# Revit family: ZETA_Коробка_Клемная_КЗНА-48_IP43
name_source: partatom
category: Электрические приборы
units: mm (PartAtom-declared; Revit-internal decimal feet)

## family parameters
Всегда вертикально = Нет
На основе рабочей плоскости = Да
Общий = Нет
При загрузке вырезать с полостями = Нет
Размер круглого соединителя = Использовать диаметр
Сохранять ориентацию аннотаций = Нет
Тип детали = Нормальный
Точка принадлежности помещению = Да

## types (2) — shared parameters
ADSK_URL документации изделия = https://nzeta.ru
ADSK_URL страницы изделия = https://nzeta.ru
ADSK_Версия Revit = 2021
ADSK_Версия семейства = v.1
ADSK_Единица измерения = шт
ADSK_Завод-изготовитель = АО «ЗЭТА»
ADSK_Классификация нагрузок = Прочее
ADSK_Код изделия = zeta30313
ADSK_Количество = 1
ADSK_Количество фаз = 1
ADSK_Количество фаз числовое = 1
ADSK_Коэффициент мощности = 1
ADSK_Марка = KK КЗНА-48 У3 IP43
ADSK_Масса = 5.67
ADSK_Масса_Текст = 5,67
ADSK_Материал наименование = Сталь оцинкованная
ADSK_Наименование = Коробка с зажимами наборными КЗНА-48 У3 IP43 ГОФРОМАТИК
ADSK_Наименование краткое = КЗНА-48
ADSK_Напряжение = 230 В
ADSK_Номинальная мощность = 0 Вт
ADSK_Обозначение = KK
ADSK_Полная мощность = 0 В·А
ADSK_Размер_Высота = 107 мм
ADSK_Размер_Длина = 345 мм
ADSK_Размер_Ширина = 266 мм
ADSK_Степень защиты_IP = IP43
ADSK_Ток = 0 А
D1 = 25 мм
D2 = 32 мм
D3 = 20 мм
D4 = 40 мм
URL = https://nzeta.ru
Изготавливается по = ТУ 27.33.13.120-047-99856433-2020
Изготовитель = АО «ЗЭТА»
Климатическое исполнение = У3
Крышка_Длина = 190 мм
Крышка_Ширина = 160 мм
Напряжение переменного тока = 660 В
Напряжение постоянного тока = 440 В
Номинальный ток = до 25A
Описание = Коробки клеммные соединительные КМ43 и КМ65 предназначены для
соединения и разветвления силовых электрических цепей и цепей КИПиА,
выполняемых контрольными и силовыми кабелями с алюминиевыми или медными
жилами сечением 1,5-4мм2.
Отметка по умолчанию = 1219 мм
Сертификат = RU C-RU.АД84.В.00192/20
Сечение жил до = 4мм2
Температура эксплуатации = от -40°С до +60°С
УГО_Высота = 5 мм
УГО_Ширина = 10 мм
zero-valued in all types: ADSK_Номер линии

## type names (no varying parameters)
- КЗНА_48
- КЗНА_48_IP43

## geometry (parser evidence)
native form markers: Sweep x1
no freeform markers — native parametric forms only
